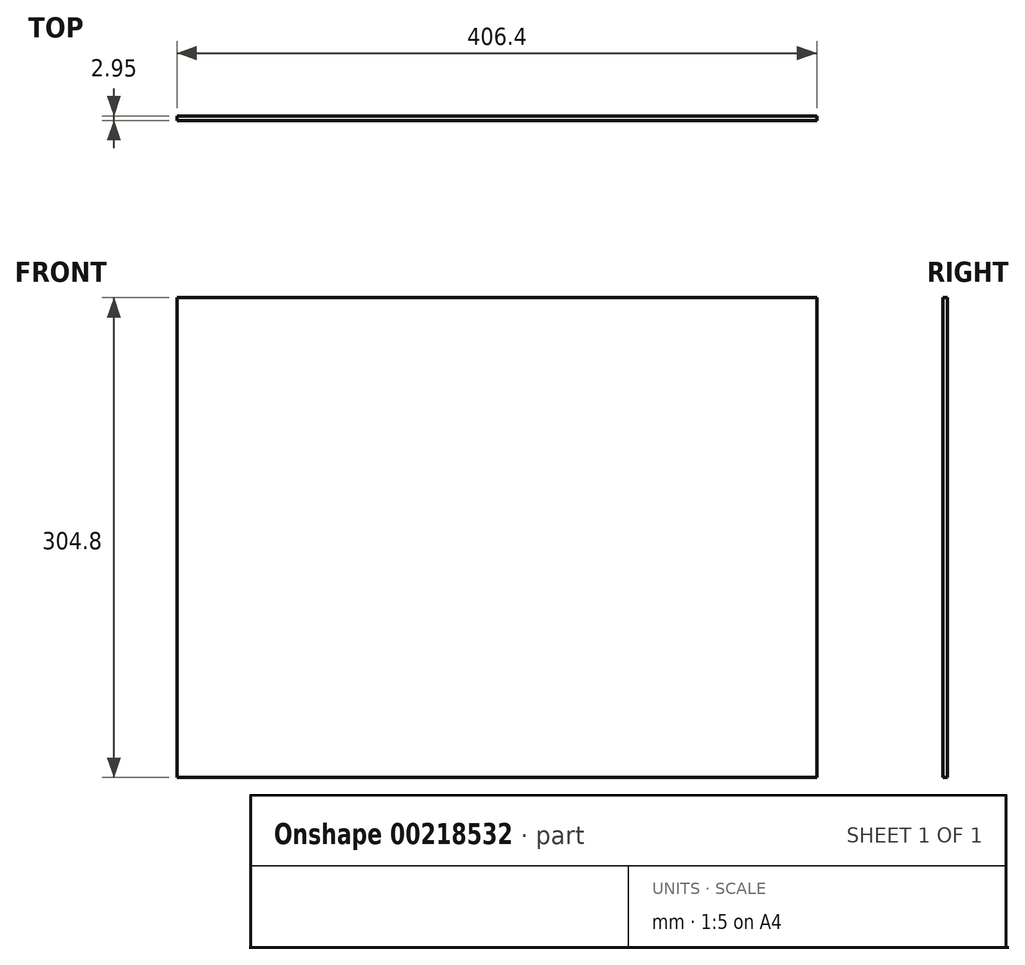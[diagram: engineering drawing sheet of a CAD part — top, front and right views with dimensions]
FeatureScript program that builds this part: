
annotation { "Feature Type Name" : "Feature", "Feature Type Description" : "" }
export const myFeature = defineFeature(function(context is Context, id is Id, definition is map)
    precondition{}
    {
        {
            assignVariable(context, id + "F0", {"name" : "THK", "anyValue" : 2.95 * mm});
        }
        {
            var Q0;
            Q0=qCreatedBy(makeId("Front.planeOp"),FACE);
            var sketch = newSketch(context, id + "F1", { "sketchPlane" : qUnion([Q0])});
            skLineSegment(sketch, "E0.bottom", {"start": v(174.7, 168.78) * mm, "end": v(-231.7, 168.78) * mm});
            skLineSegment(sketch, "E0.top", {"start": v(174.7, -136.02) * mm, "end": v(-231.7, -136.02) * mm});
            skLineSegment(sketch, "E0.left", {"start": v(174.7, 168.78) * mm, "end": v(174.7, -136.02) * mm});
            skLineSegment(sketch, "E0.right", {"start": v(-231.7, 168.78) * mm, "end": v(-231.7, -136.02) * mm});
            skSolve(sketch);
        }
        {
            var Q0;
            Q0 = qSketchRegion(id + "F1", true);
            extrude(context, id + "F2", {"entities" : qUnion([Q0]), "depth" : getVariable(context, 'THK')});
        }
    });
